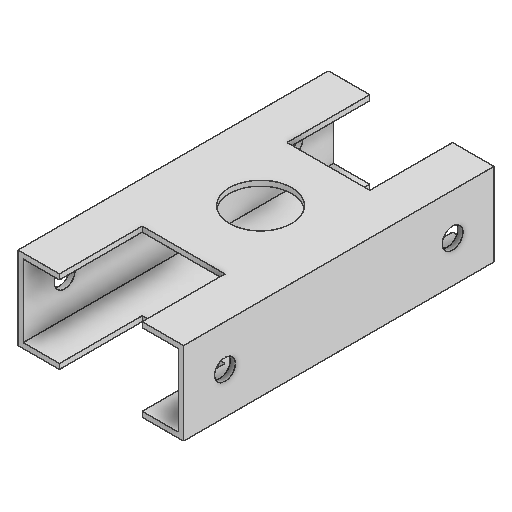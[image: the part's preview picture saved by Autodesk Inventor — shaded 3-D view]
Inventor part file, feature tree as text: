
AUTODESK INVENTOR PART (.ipt)
format: ipt  version: 2025.2 (Build 292293000, 293)  size: 164,352 bytes
history: native  units: in
note: dims shown in document units (in); Inventor stores cm internally (conversion verified against a paired STEP export)
features: extrude x3, sketch x3
ambient origin geometry x8: Origin, YZ Plane, XZ Plane, XY Plane, X Axis, Y Axis, Z Axis, Center Point
bodies: Solid1 (feature_tree)
feature tree (6):
  extrude  "Extrusion1"  Depth=1.0in
  extrude  "Extrusion2"  Depth=0.0625in
  extrude  "Extrusion3"  Depth=0.0625in
  sketch  "Sketch1"  dims[d0=2.0in d1=1.0in]
  sketch  "Sketch2"  dims[d2=0.0625in d3=0.0625in]
  sketch  "Sketch3"  dims[d4=0.0625in d5=0.0625in d6=3.75in d7=0.0in d8=0.75in d9=1.0in d10=1.82in d11=4.6in d12=0.0in d13=1.0in d14=1.0in d15=1.0in d16=1.0in d17=0.25in d18=0.5in d19=0.5in d20=0.25in d21=0.5in d22=0.5in d23=0.0in d24=0.0in]
